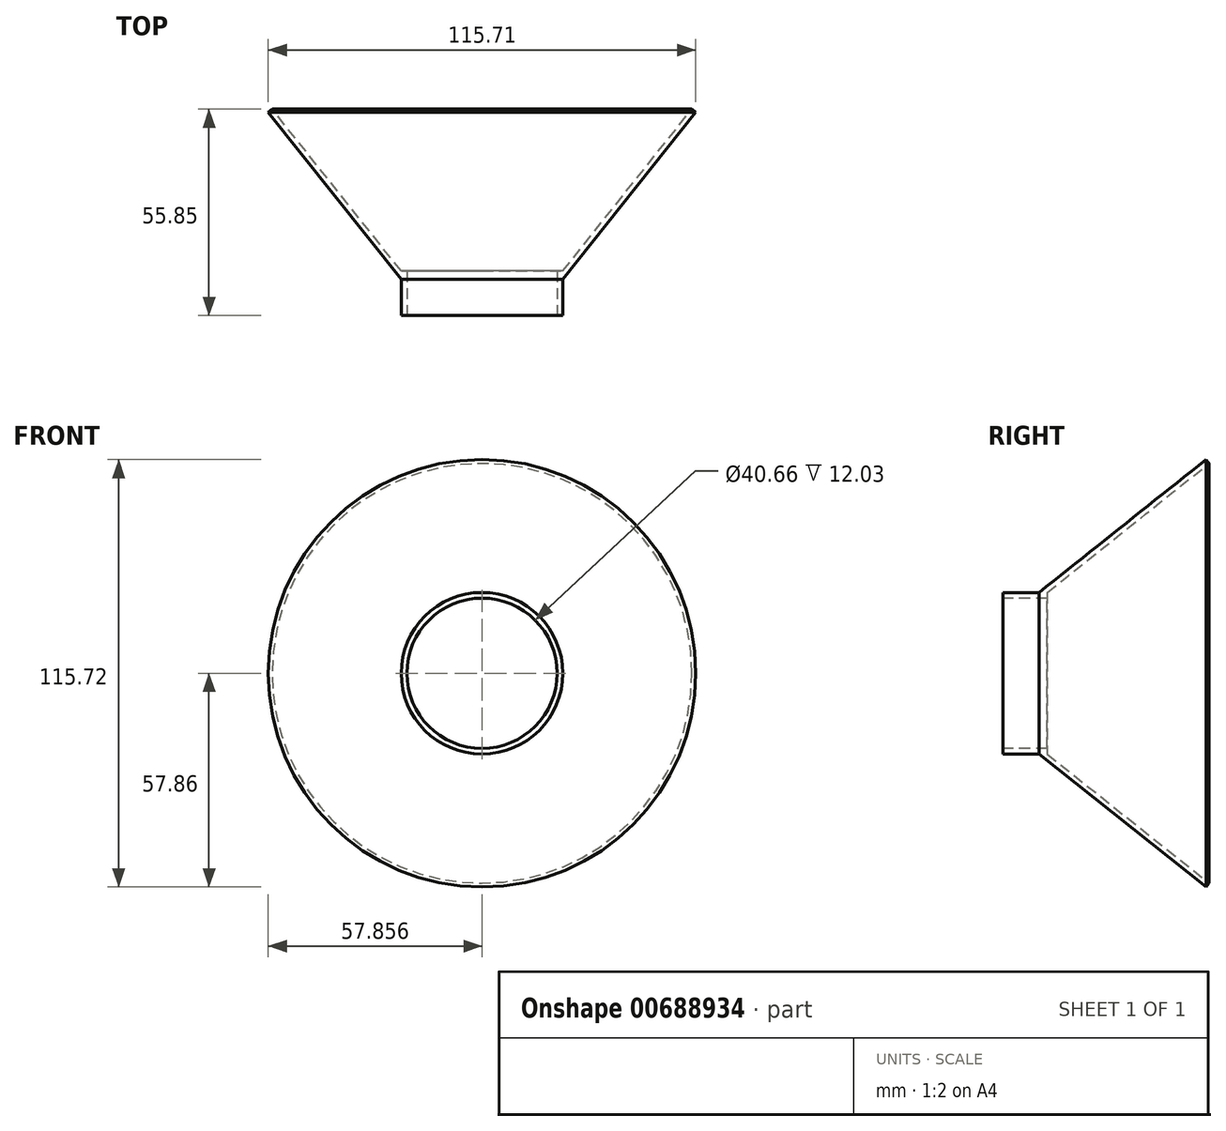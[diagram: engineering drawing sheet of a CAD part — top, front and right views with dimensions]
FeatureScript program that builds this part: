
annotation { "Feature Type Name" : "Feature", "Feature Type Description" : "" }
export const myFeature = defineFeature(function(context is Context, id is Id, definition is map)
    precondition{}
    {
        {
            var Q0;
            Q0=qCreatedBy(makeId("Top.planeOp"),FACE);
            var sketch = newSketch(context, id + "F0", { "sketchPlane" : qUnion([Q0])});
            skLineSegment(sketch, "E0", {"start": v(0, 2.2) * mm, "end": v(-21.86, 2.2) * mm});
            skLineSegment(sketch, "E1", {"start": v(-21.86, 2.2) * mm, "end": v(-21.86, -9.83) * mm});
            skLineSegment(sketch, "E2", {"start": v(-21.86, -9.83) * mm, "end": v(0, -9.83) * mm});
            skLineSegment(sketch, "E3", {"start": v(0, -9.83) * mm, "end": v(0, 0) * mm});
            skLineSegment(sketch, "E4", {"start": v(0, 0) * mm, "end": v(36, 45.16) * mm});
            skLineSegment(sketch, "E5", {"start": v(0, 2.2) * mm, "end": v(34.93, 46.02) * mm});
            skLineSegment(sketch, "E6", {"start": v(36, 45.16) * mm, "end": v(34.93, 46.02) * mm});
            skSolve(sketch);
        }
        {
            var Q0;
            Q0 = qSketchRegion(id + "F0", true);
            var Q1;
            Q1=sQuery(id+"F0.wireOp",EDGE,"E1");
            revolve(context, id + "F1", {"entities" : qUnion([Q0]), "axis" : qUnion([Q1]), "revolveType" : RevolveType.FULL});
        }
        {
            var Q0;
            Q0=makeQuery(id+"F1.opRevolve","SWEPT_FACE",FACE,{"disambiguationData":[OSD([sQuery(id+"F0.wireOp",EDGE,"E2")])]});
            var sketch = newSketch(context, id + "F2", { "sketchPlane" : qUnion([Q0])});
            skCircle(sketch, "E7", {"center": v(-21.86, 0) * mm, "radius": 20.33 * mm});
            skSolve(sketch);
        }
        {
            var Q0;
            Q0 = qSketchRegion(id + "F2", true);
            extrude(context, id + "F3", {"entities" : qUnion([Q0]), "operationType" : NewBodyOperationType.REMOVE, "oppositeDirection" : true, "depth" : 76.2 * mm, "offsetDistance" : 25.4 * mm});
        }
    });
